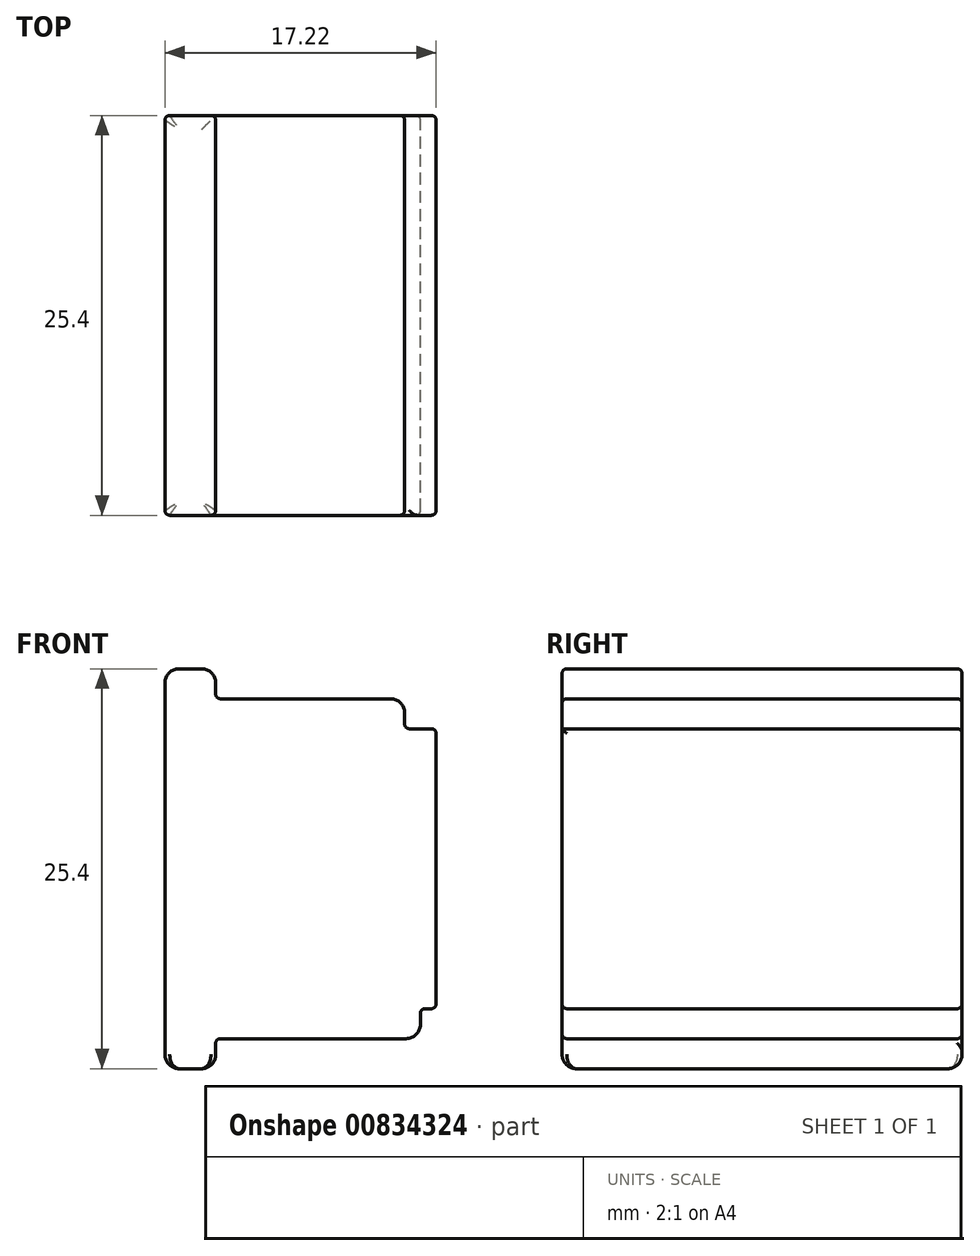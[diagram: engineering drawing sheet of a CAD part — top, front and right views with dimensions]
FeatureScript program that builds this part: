
annotation { "Feature Type Name" : "Feature", "Feature Type Description" : "" }
export const myFeature = defineFeature(function(context is Context, id is Id, definition is map)
    precondition{}
    {
        {
            var Q0;
            Q0=qCreatedBy(makeId("Front.planeOp"),FACE);
            var sketch = newSketch(context, id + "F0", { "sketchPlane" : qUnion([Q0])});
            skLineSegment(sketch, "E0", {"start": v(0, 0) * mm, "end": v(2, 0) * mm});
            skLineSegment(sketch, "E1", {"start": v(16, 3.81) * mm, "end": v(16, 21.59) * mm});
            skLineSegment(sketch, "E2", {"start": v(0, 25.4) * mm, "end": v(0, 0) * mm});
            skLineSegment(sketch, "E3", {"start": v(2, 25.4) * mm, "end": v(2, 23.5) * mm});
            skLineSegment(sketch, "E4", {"start": v(14, 23.5) * mm, "end": v(2, 23.5) * mm});
            skLineSegment(sketch, "E5", {"start": v(2, 25.4) * mm, "end": v(0, 25.4) * mm});
            skLineSegment(sketch, "E6", {"start": v(15, 1.9) * mm, "end": v(2, 1.9) * mm});
            skLineSegment(sketch, "E7", {"start": v(2, 1.9) * mm, "end": v(2, 0) * mm});
            skLineSegment(sketch, "E8", {"start": v(14, 23.5) * mm, "end": v(14, 21.59) * mm});
            skLineSegment(sketch, "E9", {"start": v(14, 21.59) * mm, "end": v(16, 21.59) * mm});
            skLineSegment(sketch, "E10", {"start": v(15, 1.9) * mm, "end": v(15, 3.81) * mm});
            skLineSegment(sketch, "E11", {"start": v(15, 3.81) * mm, "end": v(16, 3.81) * mm});
            skLineSegment(sketch, "E12", {"start": v(-23.63, -15.72) * mm, "end": v(-23.63, -27.72) * mm});
            skLineSegment(sketch, "E13", {"start": v(-23.63, -21.72) * mm, "end": v(26.37, -21.72) * mm});
            skLineSegment(sketch, "E14", {"start": v(-23.63, -15.72) * mm, "end": v(-9.93, -15.72) * mm});
            skArc(sketch, "E15", {"start": v(-9.93, -15.72) * mm, "mid": v(-9.36, -15.48) * mm, "end": v(-9.13, -14.92) * mm});
            skLineSegment(sketch, "E16", {"start": v(-9.13, -14.92) * mm, "end": v(-9.13, -14.78) * mm});
            skArc(sketch, "E17", {"start": v(-9.13, -14.78) * mm, "mid": v(-8.98, -14.43) * mm, "end": v(-8.63, -14.28) * mm});
            skLineSegment(sketch, "E18", {"start": v(-8.63, -14.28) * mm, "end": v(-7.63, -14.28) * mm});
            skArc(sketch, "E19", {"start": v(-7.63, -14.28) * mm, "mid": v(-7.27, -14.43) * mm, "end": v(-7.13, -14.78) * mm});
            skLineSegment(sketch, "E20", {"start": v(-7.13, -14.78) * mm, "end": v(-7.13, -15.04) * mm});
            skArc(sketch, "E21", {"start": v(-7.13, -15.04) * mm, "mid": v(-6.9, -15.6) * mm, "end": v(-6.33, -15.84) * mm});
            skLineSegment(sketch, "E22", {"start": v(-6.33, -15.84) * mm, "end": v(-5.33, -15.84) * mm});
            skArc(sketch, "E23", {"start": v(-5.33, -15.84) * mm, "mid": v(-5.17, -15.85) * mm, "end": v(-5.02, -15.9) * mm});
            skLineSegment(sketch, "E24", {"start": v(-5.02, -15.9) * mm, "end": v(-1.39, -17.07) * mm});
            skArc(sketch, "E25", {"start": v(-1.39, -17.07) * mm, "mid": v(-0.93, -17.18) * mm, "end": v(-0.46, -17.22) * mm});
            skLineSegment(sketch, "E26", {"start": v(-0.46, -17.22) * mm, "end": v(1.92, -17.22) * mm});
            skArc(sketch, "E27", {"start": v(1.92, -17.22) * mm, "mid": v(2.5, -17.03) * mm, "end": v(2.87, -16.53) * mm});
            skArc(sketch, "E28", {"start": v(2.87, -16.53) * mm, "mid": v(3.24, -16.03) * mm, "end": v(3.82, -15.84) * mm});
            skLineSegment(sketch, "E29", {"start": v(3.82, -15.84) * mm, "end": v(4.47, -15.84) * mm});
            skArc(sketch, "E30", {"start": v(4.47, -15.84) * mm, "mid": v(5.1, -16.1) * mm, "end": v(5.37, -16.74) * mm});
            skLineSegment(sketch, "E31", {"start": v(5.37, -16.74) * mm, "end": v(5.37, -16.84) * mm});
            skArc(sketch, "E32", {"start": v(5.37, -16.84) * mm, "mid": v(5.64, -17.48) * mm, "end": v(6.27, -17.74) * mm});
            skLineSegment(sketch, "E33", {"start": v(6.27, -17.74) * mm, "end": v(7.97, -17.74) * mm});
            skArc(sketch, "E34", {"start": v(7.97, -17.74) * mm, "mid": v(8.6, -17.48) * mm, "end": v(8.87, -16.84) * mm});
            skLineSegment(sketch, "E35", {"start": v(8.87, -16.84) * mm, "end": v(8.87, -16.74) * mm});
            skArc(sketch, "E36", {"start": v(8.87, -16.74) * mm, "mid": v(9.14, -16.1) * mm, "end": v(9.77, -15.84) * mm});
            skLineSegment(sketch, "E37", {"start": v(9.77, -15.84) * mm, "end": v(15.93, -15.84) * mm});
            skArc(sketch, "E38", {"start": v(15.93, -15.84) * mm, "mid": v(16.27, -15.86) * mm, "end": v(16.6, -15.92) * mm});
            skLineSegment(sketch, "E39", {"start": v(16.6, -15.92) * mm, "end": v(19.3, -16.54) * mm});
            skArc(sketch, "E40", {"start": v(19.3, -16.54) * mm, "mid": v(19.63, -16.6) * mm, "end": v(19.97, -16.62) * mm});
            skLineSegment(sketch, "E41", {"start": v(19.97, -16.62) * mm, "end": v(26.37, -16.62) * mm});
            skLineSegment(sketch, "E42", {"start": v(-23.63, -16.62) * mm, "end": v(-9.93, -16.62) * mm});
            skArc(sketch, "E43", {"start": v(-9.93, -16.62) * mm, "mid": v(-8.82, -16.2) * mm, "end": v(-8.25, -15.18) * mm});
            skLineSegment(sketch, "E44", {"start": v(-8.25, -15.18) * mm, "end": v(-8.02, -15.18) * mm});
            skArc(sketch, "E45", {"start": v(-8.02, -15.18) * mm, "mid": v(-7.48, -16.3) * mm, "end": v(-6.33, -16.74) * mm});
            skLineSegment(sketch, "E46", {"start": v(-6.33, -16.74) * mm, "end": v(-5.33, -16.74) * mm});
            skArc(sketch, "E47", {"start": v(-5.33, -16.74) * mm, "mid": v(-5.31, -16.74) * mm, "end": v(-5.3, -16.75) * mm});
            skLineSegment(sketch, "E48", {"start": v(-5.3, -16.75) * mm, "end": v(-1.67, -17.93) * mm});
            skArc(sketch, "E49", {"start": v(-1.67, -17.93) * mm, "mid": v(-1.07, -18.07) * mm, "end": v(-0.46, -18.12) * mm});
            skLineSegment(sketch, "E50", {"start": v(-0.46, -18.12) * mm, "end": v(1.92, -18.12) * mm});
            skArc(sketch, "E51", {"start": v(1.92, -18.12) * mm, "mid": v(3.04, -17.76) * mm, "end": v(3.73, -16.8) * mm});
            skArc(sketch, "E52", {"start": v(3.73, -16.8) * mm, "mid": v(3.76, -16.76) * mm, "end": v(3.82, -16.74) * mm});
            skLineSegment(sketch, "E53", {"start": v(3.82, -16.74) * mm, "end": v(4.47, -16.74) * mm});
            skLineSegment(sketch, "E54", {"start": v(4.47, -16.74) * mm, "end": v(4.47, -16.84) * mm});
            skArc(sketch, "E55", {"start": v(4.47, -16.84) * mm, "mid": v(5, -18.11) * mm, "end": v(6.27, -18.64) * mm});
            skLineSegment(sketch, "E56", {"start": v(6.27, -18.64) * mm, "end": v(7.97, -18.64) * mm});
            skArc(sketch, "E57", {"start": v(7.97, -18.64) * mm, "mid": v(9.25, -18.11) * mm, "end": v(9.77, -16.84) * mm});
            skLineSegment(sketch, "E58", {"start": v(9.77, -16.84) * mm, "end": v(9.77, -16.74) * mm});
            skLineSegment(sketch, "E59", {"start": v(9.77, -16.74) * mm, "end": v(15.93, -16.74) * mm});
            skArc(sketch, "E60", {"start": v(15.93, -16.74) * mm, "mid": v(16.17, -16.75) * mm, "end": v(16.4, -16.8) * mm});
            skLineSegment(sketch, "E61", {"start": v(16.4, -16.8) * mm, "end": v(19.1, -17.42) * mm});
            skArc(sketch, "E62", {"start": v(19.1, -17.42) * mm, "mid": v(19.53, -17.5) * mm, "end": v(19.97, -17.52) * mm});
            skLineSegment(sketch, "E63", {"start": v(19.97, -17.52) * mm, "end": v(26.37, -17.52) * mm});
            skLineSegment(sketch, "E64", {"start": v(26.37, -26.82) * mm, "end": v(26.37, -16.62) * mm});
            skLineSegment(sketch, "E65", {"start": v(-23.63, -27.72) * mm, "end": v(-9.93, -27.72) * mm});
            skArc(sketch, "E66", {"start": v(-9.93, -27.72) * mm, "mid": v(-9.36, -27.95) * mm, "end": v(-9.13, -28.52) * mm});
            skLineSegment(sketch, "E67", {"start": v(-9.13, -28.52) * mm, "end": v(-9.13, -28.65) * mm});
            skArc(sketch, "E68", {"start": v(-9.13, -28.65) * mm, "mid": v(-8.98, -29) * mm, "end": v(-8.63, -29.15) * mm});
            skLineSegment(sketch, "E69", {"start": v(-8.63, -29.15) * mm, "end": v(-7.63, -29.15) * mm});
            skArc(sketch, "E70", {"start": v(-7.63, -29.15) * mm, "mid": v(-7.27, -29) * mm, "end": v(-7.13, -28.65) * mm});
            skLineSegment(sketch, "E71", {"start": v(-7.13, -28.65) * mm, "end": v(-7.13, -28.4) * mm});
            skArc(sketch, "E72", {"start": v(-7.13, -28.4) * mm, "mid": v(-6.9, -27.83) * mm, "end": v(-6.33, -27.6) * mm});
            skLineSegment(sketch, "E73", {"start": v(-6.33, -27.6) * mm, "end": v(-5.33, -27.6) * mm});
            skArc(sketch, "E74", {"start": v(-5.33, -27.6) * mm, "mid": v(-5.17, -27.58) * mm, "end": v(-5.02, -27.54) * mm});
            skLineSegment(sketch, "E75", {"start": v(-5.02, -27.54) * mm, "end": v(-1.39, -26.36) * mm});
            skArc(sketch, "E76", {"start": v(-1.39, -26.36) * mm, "mid": v(-0.93, -26.25) * mm, "end": v(-0.46, -26.22) * mm});
            skLineSegment(sketch, "E77", {"start": v(-0.46, -26.22) * mm, "end": v(1.92, -26.22) * mm});
            skArc(sketch, "E78", {"start": v(1.92, -26.22) * mm, "mid": v(2.5, -26.4) * mm, "end": v(2.87, -26.9) * mm});
            skArc(sketch, "E79", {"start": v(2.87, -26.9) * mm, "mid": v(3.24, -27.4) * mm, "end": v(3.82, -27.6) * mm});
            skLineSegment(sketch, "E80", {"start": v(3.82, -27.6) * mm, "end": v(4.47, -27.6) * mm});
            skArc(sketch, "E81", {"start": v(4.47, -27.6) * mm, "mid": v(5.1, -27.33) * mm, "end": v(5.37, -26.7) * mm});
            skLineSegment(sketch, "E82", {"start": v(5.37, -26.7) * mm, "end": v(5.37, -26.6) * mm});
            skArc(sketch, "E83", {"start": v(5.37, -26.6) * mm, "mid": v(5.64, -25.95) * mm, "end": v(6.27, -25.7) * mm});
            skLineSegment(sketch, "E84", {"start": v(6.27, -25.7) * mm, "end": v(7.97, -25.7) * mm});
            skArc(sketch, "E85", {"start": v(7.97, -25.7) * mm, "mid": v(8.6, -25.95) * mm, "end": v(8.87, -26.6) * mm});
            skLineSegment(sketch, "E86", {"start": v(8.87, -26.6) * mm, "end": v(8.87, -26.7) * mm});
            skArc(sketch, "E87", {"start": v(8.87, -26.7) * mm, "mid": v(9.14, -27.33) * mm, "end": v(9.77, -27.6) * mm});
            skLineSegment(sketch, "E88", {"start": v(9.77, -27.6) * mm, "end": v(15.93, -27.6) * mm});
            skArc(sketch, "E89", {"start": v(15.93, -27.6) * mm, "mid": v(16.27, -27.57) * mm, "end": v(16.6, -27.51) * mm});
            skLineSegment(sketch, "E90", {"start": v(16.6, -27.51) * mm, "end": v(19.3, -26.9) * mm});
            skArc(sketch, "E91", {"start": v(19.3, -26.9) * mm, "mid": v(19.63, -26.84) * mm, "end": v(19.97, -26.82) * mm});
            skLineSegment(sketch, "E92", {"start": v(19.97, -26.82) * mm, "end": v(26.37, -26.82) * mm});
            skLineSegment(sketch, "E93", {"start": v(-23.63, -26.82) * mm, "end": v(-9.93, -26.82) * mm});
            skArc(sketch, "E94", {"start": v(-9.93, -26.82) * mm, "mid": v(-8.82, -27.22) * mm, "end": v(-8.25, -28.25) * mm});
            skLineSegment(sketch, "E95", {"start": v(-8.25, -28.25) * mm, "end": v(-8.02, -28.25) * mm});
            skArc(sketch, "E96", {"start": v(-8.02, -28.25) * mm, "mid": v(-7.48, -27.14) * mm, "end": v(-6.33, -26.7) * mm});
            skLineSegment(sketch, "E97", {"start": v(-6.33, -26.7) * mm, "end": v(-5.33, -26.7) * mm});
            skArc(sketch, "E98", {"start": v(-5.33, -26.7) * mm, "mid": v(-5.31, -26.7) * mm, "end": v(-5.3, -26.69) * mm});
            skLineSegment(sketch, "E99", {"start": v(-5.3, -26.69) * mm, "end": v(-1.67, -25.5) * mm});
            skArc(sketch, "E100", {"start": v(-1.67, -25.5) * mm, "mid": v(-1.07, -25.36) * mm, "end": v(-0.46, -25.32) * mm});
            skLineSegment(sketch, "E101", {"start": v(-0.46, -25.32) * mm, "end": v(1.92, -25.32) * mm});
            skArc(sketch, "E102", {"start": v(1.92, -25.32) * mm, "mid": v(3.04, -25.68) * mm, "end": v(3.73, -26.62) * mm});
            skArc(sketch, "E103", {"start": v(3.73, -26.62) * mm, "mid": v(3.76, -26.67) * mm, "end": v(3.82, -26.7) * mm});
            skLineSegment(sketch, "E104", {"start": v(3.82, -26.7) * mm, "end": v(4.47, -26.7) * mm});
            skLineSegment(sketch, "E105", {"start": v(4.47, -26.7) * mm, "end": v(4.47, -26.6) * mm});
            skArc(sketch, "E106", {"start": v(4.47, -26.6) * mm, "mid": v(5, -25.32) * mm, "end": v(6.27, -24.8) * mm});
            skLineSegment(sketch, "E107", {"start": v(6.27, -24.8) * mm, "end": v(7.97, -24.8) * mm});
            skArc(sketch, "E108", {"start": v(7.97, -24.8) * mm, "mid": v(9.25, -25.32) * mm, "end": v(9.77, -26.6) * mm});
            skLineSegment(sketch, "E109", {"start": v(9.77, -26.6) * mm, "end": v(9.77, -26.7) * mm});
            skLineSegment(sketch, "E110", {"start": v(9.77, -26.7) * mm, "end": v(15.93, -26.7) * mm});
            skArc(sketch, "E111", {"start": v(15.93, -26.7) * mm, "mid": v(16.17, -26.68) * mm, "end": v(16.4, -26.64) * mm});
            skLineSegment(sketch, "E112", {"start": v(16.4, -26.64) * mm, "end": v(19.1, -26.02) * mm});
            skArc(sketch, "E113", {"start": v(19.1, -26.02) * mm, "mid": v(19.53, -25.94) * mm, "end": v(19.97, -25.92) * mm});
            skLineSegment(sketch, "E114", {"start": v(19.97, -25.92) * mm, "end": v(26.37, -25.92) * mm});
            skLineSegment(sketch, "E115", {"start": v(19.97, -16.62) * mm, "end": v(19.97, -26.82) * mm});
            skLineSegment(sketch, "E116", {"start": v(19.3, -16.54) * mm, "end": v(19.3, -26.9) * mm});
            skLineSegment(sketch, "E117", {"start": v(15.93, -15.84) * mm, "end": v(15.93, -27.6) * mm});
            skLineSegment(sketch, "E118", {"start": v(16.6, -15.92) * mm, "end": v(16.6, -27.51) * mm});
            skLineSegment(sketch, "E119", {"start": v(1.92, -17.22) * mm, "end": v(1.92, -26.22) * mm});
            skLineSegment(sketch, "E120", {"start": v(-9.93, -15.72) * mm, "end": v(-9.93, -27.72) * mm});
            skLineSegment(sketch, "E121", {"start": v(5.37, -16.84) * mm, "end": v(5.37, -26.6) * mm});
            skLineSegment(sketch, "E122", {"start": v(8.87, -16.84) * mm, "end": v(8.87, -26.6) * mm});
            skLineSegment(sketch, "E123", {"start": v(9.77, -15.84) * mm, "end": v(9.77, -27.6) * mm});
            skLineSegment(sketch, "E124", {"start": v(-1.39, -17.07) * mm, "end": v(-1.39, -26.36) * mm});
            skLineSegment(sketch, "E125", {"start": v(-0.46, -17.22) * mm, "end": v(-0.46, -26.22) * mm});
            skLineSegment(sketch, "E126", {"start": v(-5.02, -15.9) * mm, "end": v(-5.02, -27.54) * mm});
            skLineSegment(sketch, "E127", {"start": v(-5.33, -15.84) * mm, "end": v(-5.33, -27.6) * mm});
            skLineSegment(sketch, "E128", {"start": v(-6.33, -15.84) * mm, "end": v(-6.33, -27.6) * mm});
            skLineSegment(sketch, "E129", {"start": v(0, 25.4) * mm, "end": v(-1.22, 25.4) * mm});
            skLineSegment(sketch, "E130", {"start": v(-1.22, 25.4) * mm, "end": v(-1.22, 0) * mm});
            skLineSegment(sketch, "E131", {"start": v(-1.22, 0) * mm, "end": v(0, 0) * mm});
            skSolve(sketch);
        }
        {
            var Q0;
            Q0=makeQuery(id+"F0.imprint","IMPRINT",FACE,{"disambiguationData":[TD([[makeQuery(id+"F0.imprint","IMPRINT",EDGE,{"derivedFrom":sQuery(id+"F0.wireOp",EDGE,"E0")}),1.0]])]});
            var Q1;
            Q1=makeQuery(id+"F0.imprint","IMPRINT",FACE,{"disambiguationData":[TD([[makeQuery(id+"F0.imprint","IMPRINT",EDGE,{"derivedFrom":sQuery(id+"F0.wireOp",EDGE,"E2")}),-1.0]])]});
            extrude(context, id + "F1", {"entities" : qUnion([Q0, Q1]), "endBound" : BoundingType.SYMMETRIC, "depth" : 25.4 * mm, "offsetDistance" : 25.4 * mm});
        }
        {
            var Q0;
            Q0=makeQuery(id+"F1.opExtrude","SWEPT_EDGE",EDGE,{"disambiguationData":[OSD([sQuery(id+"F0.wireOp",EDGE,"E3"),sQuery(id+"F0.wireOp",EDGE,"E4")])]});
            var Q1;
            Q1=makeQuery(id+"F1.opExtrude","CAP_EDGE",EDGE,{"disambiguationData":[OSD([sQuery(id+"F0.wireOp",EDGE,"E3")])],"isStart":false});
            var Q2;
            Q2=makeQuery(id+"F1.opExtrude","CAP_EDGE",EDGE,{"disambiguationData":[OSD([sQuery(id+"F0.wireOp",EDGE,"E5"),sQuery(id+"F0.wireOp",EDGE,"E129")])],"isStart":false});
            var Q3;
            Q3=makeQuery(id+"F1.opExtrude","CAP_EDGE",EDGE,{"disambiguationData":[OSD([sQuery(id+"F0.wireOp",EDGE,"E130")])],"isStart":false});
            var Q4;
            Q4=makeQuery(id+"F1.opExtrude","CAP_EDGE",EDGE,{"disambiguationData":[OSD([sQuery(id+"F0.wireOp",EDGE,"E4")])],"isStart":false});
            var Q5;
            Q5=makeQuery(id+"F1.opExtrude","CAP_EDGE",EDGE,{"disambiguationData":[OSD([sQuery(id+"F0.wireOp",EDGE,"E8")])],"isStart":false});
            var Q6;
            Q6=makeQuery(id+"F1.opExtrude","SWEPT_EDGE",EDGE,{"disambiguationData":[OSD([sQuery(id+"F0.wireOp",EDGE,"E8"),sQuery(id+"F0.wireOp",EDGE,"E9")])]});
            var Q7;
            Q7=makeQuery(id+"F1.opExtrude","SWEPT_EDGE",EDGE,{"disambiguationData":[OSD([sQuery(id+"F0.wireOp",EDGE,"E1"),sQuery(id+"F0.wireOp",EDGE,"E9")])]});
            var Q8;
            Q8=makeQuery(id+"F1.opExtrude","CAP_EDGE",EDGE,{"disambiguationData":[OSD([sQuery(id+"F0.wireOp",EDGE,"E1")])],"isStart":false});
            var Q9;
            Q9=makeQuery(id+"F1.opExtrude","SWEPT_EDGE",EDGE,{"disambiguationData":[OSD([sQuery(id+"F0.wireOp",EDGE,"E10"),sQuery(id+"F0.wireOp",EDGE,"E11")])]});
            var Q10;
            Q10=makeQuery(id+"F1.opExtrude","CAP_EDGE",EDGE,{"disambiguationData":[OSD([sQuery(id+"F0.wireOp",EDGE,"E11")])],"isStart":false});
            var Q11;
            Q11=makeQuery(id+"F1.opExtrude","CAP_EDGE",EDGE,{"disambiguationData":[OSD([sQuery(id+"F0.wireOp",EDGE,"E10")])],"isStart":false});
            var Q12;
            Q12=makeQuery(id+"F1.opExtrude","CAP_EDGE",EDGE,{"disambiguationData":[OSD([sQuery(id+"F0.wireOp",EDGE,"E6")])],"isStart":false});
            var Q13;
            Q13=makeQuery(id+"F1.opExtrude","CAP_EDGE",EDGE,{"disambiguationData":[OSD([sQuery(id+"F0.wireOp",EDGE,"E7")])],"isStart":false});
            var Q14;
            Q14=makeQuery(id+"F1.opExtrude","SWEPT_EDGE",EDGE,{"disambiguationData":[OSD([sQuery(id+"F0.wireOp",EDGE,"E6"),sQuery(id+"F0.wireOp",EDGE,"E7")])]});
            var Q15;
            Q15=makeQuery(id+"F1.opExtrude","CAP_EDGE",EDGE,{"disambiguationData":[OSD([sQuery(id+"F0.wireOp",EDGE,"E1")])],"isStart":true});
            var Q16;
            Q16=makeQuery(id+"F1.opExtrude","CAP_EDGE",EDGE,{"disambiguationData":[OSD([sQuery(id+"F0.wireOp",EDGE,"E9")])],"isStart":true});
            var Q17;
            Q17=makeQuery(id+"F1.opExtrude","CAP_EDGE",EDGE,{"disambiguationData":[OSD([sQuery(id+"F0.wireOp",EDGE,"E8")])],"isStart":true});
            var Q18;
            Q18=makeQuery(id+"F1.opExtrude","CAP_EDGE",EDGE,{"disambiguationData":[OSD([sQuery(id+"F0.wireOp",EDGE,"E4")])],"isStart":true});
            var Q19;
            Q19=makeQuery(id+"F1.opExtrude","CAP_EDGE",EDGE,{"disambiguationData":[OSD([sQuery(id+"F0.wireOp",EDGE,"E3")])],"isStart":true});
            var Q20;
            Q20=makeQuery(id+"F1.opExtrude","CAP_EDGE",EDGE,{"disambiguationData":[OSD([sQuery(id+"F0.wireOp",EDGE,"E5"),sQuery(id+"F0.wireOp",EDGE,"E129")])],"isStart":true});
            var Q21;
            Q21=makeQuery(id+"F1.opExtrude","CAP_EDGE",EDGE,{"disambiguationData":[OSD([sQuery(id+"F0.wireOp",EDGE,"E130")])],"isStart":true});
            var Q22;
            Q22=makeQuery(id+"F1.opExtrude","SWEPT_EDGE",EDGE,{"disambiguationData":[OSD([sQuery(id+"F0.wireOp",EDGE,"E1"),sQuery(id+"F0.wireOp",EDGE,"E11")])]});
            var Q23;
            Q23=makeQuery(id+"F1.opExtrude","CAP_EDGE",EDGE,{"disambiguationData":[OSD([sQuery(id+"F0.wireOp",EDGE,"E6")])],"isStart":true});
            var Q24;
            Q24=makeQuery(id+"F1.opExtrude","CAP_EDGE",EDGE,{"disambiguationData":[OSD([sQuery(id+"F0.wireOp",EDGE,"E10")])],"isStart":true});
            var Q25;
            Q25=makeQuery(id+"F1.opExtrude","CAP_EDGE",EDGE,{"disambiguationData":[OSD([sQuery(id+"F0.wireOp",EDGE,"E11")])],"isStart":true});
            fillet(context, id + "F2", {"entities" : qUnion([Q0, Q1, Q2, Q3, Q4, Q5, Q6, Q7, Q8, Q9, Q10, Q11, Q12, Q13, Q14, Q15, Q16, Q17, Q18, Q19, Q20, Q21, Q22, Q23, Q24, Q25]), "radius" : .3 * mm, "tangentPropagation" : true, "allowEdgeOverflow" : false});
        }
        {
            var Q0;
            Q0=makeQuery(id+"F1.opExtrude","SWEPT_EDGE",EDGE,{"disambiguationData":[OSD([sQuery(id+"F0.wireOp",EDGE,"E3"),sQuery(id+"F0.wireOp",EDGE,"E5")])]});
            var Q1;
            Q1=makeQuery(id+"F1.opExtrude","SWEPT_EDGE",EDGE,{"disambiguationData":[OSD([sQuery(id+"F0.wireOp",EDGE,"E4"),sQuery(id+"F0.wireOp",EDGE,"E8")])]});
            var Q2;
            Q2=makeQuery(id+"F1.opExtrude","SWEPT_EDGE",EDGE,{"disambiguationData":[OSD([sQuery(id+"F0.wireOp",EDGE,"E129"),sQuery(id+"F0.wireOp",EDGE,"E130")])]});
            var Q3;
            Q3=makeQuery(id+"F1.opExtrude","SWEPT_EDGE",EDGE,{"disambiguationData":[OSD([sQuery(id+"F0.wireOp",EDGE,"E130"),sQuery(id+"F0.wireOp",EDGE,"E131")])]});
            var Q4;
            Q4=makeQuery(id+"F1.opExtrude","SWEPT_EDGE",EDGE,{"disambiguationData":[OSD([sQuery(id+"F0.wireOp",EDGE,"E0"),sQuery(id+"F0.wireOp",EDGE,"E7")])]});
            var Q5;
            Q5=makeQuery(id+"F1.opExtrude","SWEPT_FACE",FACE,{"disambiguationData":[OSD([sQuery(id+"F0.wireOp",EDGE,"E10")])]});
            var Q6;
            Q6=makeQuery(id+"F1.opExtrude","SWEPT_FACE",FACE,{"disambiguationData":[OSD([sQuery(id+"F0.wireOp",EDGE,"E6")])]});
            var Q7;
            {var subQ0=sQuery(id+"F0.wireOp",EDGE,"E10");Q7=makeQuery(id+"F2.opFillet","BLEND_EDGE",EDGE,{"blendedFrom":[makeQuery(id+"F1.opExtrude","SWEPT_EDGE",EDGE,{"disambiguationData":[OSD([sQuery(id+"F0.wireOp",EDGE,"E6"),subQ0])]}),makeQuery(id+"F1.opExtrude","SWEPT_FACE",FACE,{"disambiguationData":[OSD([subQ0])]})],"blendedInto":[makeQuery(id+"F1.opExtrude","SWEPT_FACE",FACE,{"disambiguationData":[OSD([subQ0])]})]});}
            var Q8;
            {var subQ0=sQuery(id+"F0.wireOp",EDGE,"E6");Q8=makeQuery(id+"F2.opFillet","BLEND_EDGE",EDGE,{"blendedFrom":[makeQuery(id+"F1.opExtrude","SWEPT_EDGE",EDGE,{"disambiguationData":[OSD([subQ0,sQuery(id+"F0.wireOp",EDGE,"E10")])]}),makeQuery(id+"F1.opExtrude","SWEPT_FACE",FACE,{"disambiguationData":[OSD([subQ0])]})],"blendedInto":[makeQuery(id+"F1.opExtrude","SWEPT_FACE",FACE,{"disambiguationData":[OSD([subQ0])]})]});}
            fillet(context, id + "F3", {"entities" : qUnion([Q0, Q1, Q2, Q3, Q4, Q5, Q6, Q7, Q8]), "radius" : .9 * mm, "tangentPropagation" : true, "allowEdgeOverflow" : false});
        }
    });
